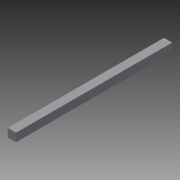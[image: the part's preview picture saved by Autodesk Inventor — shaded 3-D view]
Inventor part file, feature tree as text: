
AUTODESK INVENTOR PART (.ipt)
format: ipt  version: 2015 (Build 190159000, 159)  size: 68,096 bytes
history: native  units: in
note: dims shown in document units (in); Inventor stores cm internally (conversion verified against a paired STEP export)
features: extrude x1, sketch x1
ambient origin geometry x8: Origin, YZ Plane, XZ Plane, XY Plane, X Axis, Y Axis, Z Axis, Center Point
bodies: Solid1 (feature_tree)
feature tree (2):
  extrude  "Extrusion1"  Depth=0.75in
  sketch  "Sketch1"  dims[d0=0.75in d1=0.75in d2=14.25in d3=0.0in]
